# Revit family: Shower_Trim-DXV-Oak-Hill-D3515543X_Series
name_source: partatom
category: Plumbing Fixtures
units: mm (PartAtom-declared; Revit-internal decimal feet)

## family parameters
Cut with Voids When Loaded = No
Host = Face
OmniClass Number = 23.45.05.14.17
OmniClass Title = Showers
Part Type = Normal
Room Calculation Point = No
Round Connector Dimension = Use Diameter
Shared = Yes

## types (8) — shared parameters
ADA Compliant = Yes
Assembly Code = D2010710
CW Connection = Yes
CWFU = 3
Cold Water Connection Diameter = 1/2"
Cold Water Connection Radius = 1/4"
Compliance Certifications = Meets or Exceeds ASME A112.18.1/CSA B125.1
D35000420.191 3/2 Port Diverter Rough Valve Only = No
D35000430.191 4/3 Port Diverter Rough Valve = No
Default Elevation = 48"
Description = Oak Hill® 3/2 or 4/3 Diverter Valve Trim Only with Lever Handle
Diameter = 3"
HW Connection = Yes
HWFU = 3
Hot Water Connection Diameter = 1/2"
Hot Water Connection Radius = 1/4"
Installation Type = Wall Mount
Manufacturer = DXV
Product Documentation Link = https://lixil.cdn.celum.cloud
Product Page URL = https://www.dxv.com
Rough Valve Distance = 2 13/16"
Tempered Water Connection = Yes
Tempered Water Connection Diameter = 1/2"
Tempered Water Connection Radius = 1/4"
Type Comments = Requires Diverter Rough-in Valve D35000420 for 2-outlet discrete water flow or D35000430 for 3-outlet discrete water flow, each sold separately
URL = https://www.dxv.com
Vent Connection = No
WFU = 4
Waste Connection = No

## per-type parameters (varying)
| type | Cross Handle | Finish | Lever Handle (ADA) | Material |
| D35155430.100 | No | Cast Brass-DXV-100-Polished Chrome | Yes | Cast Brass-DXV-100-Polished Chrome |
| D35155430.144 | No | Cast Brass-DXV-144-Brushed Nickel | Yes | Cast Brass-DXV-144-Brushed Nickel |
| D35155430.150 | No | Cast Brass-DXV-150-Platinum Nickel | Yes | Cast Brass-DXV-150-Platinum Nickel |
| D35155430.427 | No | Cast Brass-DXV-427-Satin Brass | Yes | Cast Brass-DXV-427-Satin Brass |
| D35155434.100 | Yes | Cast Brass-DXV-100-Polished Chrome | No | Cast Brass-DXV-100-Polished Chrome |
| D35155434.144 | Yes | Cast Brass-DXV-144-Brushed Nickel | No | Cast Brass-DXV-144-Brushed Nickel |
| D35155434.150 | Yes | Cast Brass-DXV-150-Platinum Nickel | No | Cast Brass-DXV-150-Platinum Nickel |
| D35155434.427 | Yes | Cast Brass-DXV-427-Satin Brass | No | Cast Brass-DXV-427-Satin Brass |

note: column(s) folded — value = type name in every type: Model

## geometry (parser evidence)
native form markers: Sweep x2
no freeform markers — native parametric forms only
